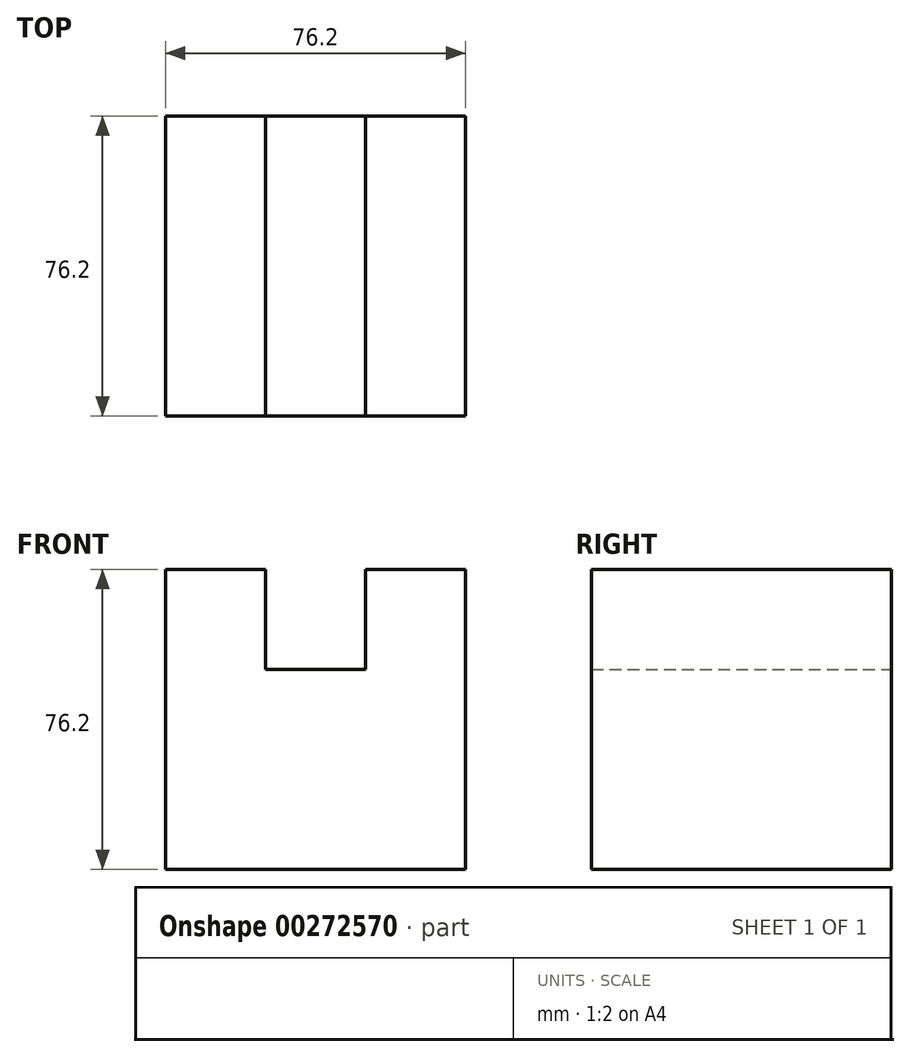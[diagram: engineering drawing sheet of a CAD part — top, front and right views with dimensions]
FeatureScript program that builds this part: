
annotation { "Feature Type Name" : "Feature", "Feature Type Description" : "" }
export const myFeature = defineFeature(function(context is Context, id is Id, definition is map)
    precondition{}
    {
        {
            var Q0;
            Q0=qCreatedBy(makeId("Front.planeOp"),FACE);
            var sketch = newSketch(context, id + "F0", { "sketchPlane" : qUnion([Q0])});
            skLineSegment(sketch, "E0", {"start": v(0, 0) * mm, "end": v(-76.2, 0) * mm});
            skLineSegment(sketch, "E1", {"start": v(-76.2, 0) * mm, "end": v(-76.2, 76.2) * mm});
            skLineSegment(sketch, "E2", {"start": v(-76.2, 76.2) * mm, "end": v(-50.8, 76.2) * mm});
            skLineSegment(sketch, "E3", {"start": v(-50.8, 76.2) * mm, "end": v(-50.8, 50.8) * mm});
            skLineSegment(sketch, "E4", {"start": v(-50.8, 50.8) * mm, "end": v(-25.4, 50.8) * mm});
            skLineSegment(sketch, "E5", {"start": v(-25.4, 50.8) * mm, "end": v(-25.4, 76.2) * mm});
            skLineSegment(sketch, "E6", {"start": v(-25.4, 76.2) * mm, "end": v(0, 76.2) * mm});
            skLineSegment(sketch, "E7", {"start": v(0, 76.2) * mm, "end": v(0, 0) * mm});
            skSolve(sketch);
        }
        {
            var Q0;
            Q0 = qSketchRegion(id + "F0", true);
            extrude(context, id + "F1", {"entities" : qUnion([Q0]), "depth" : 76.2 * mm});
        }
    });
